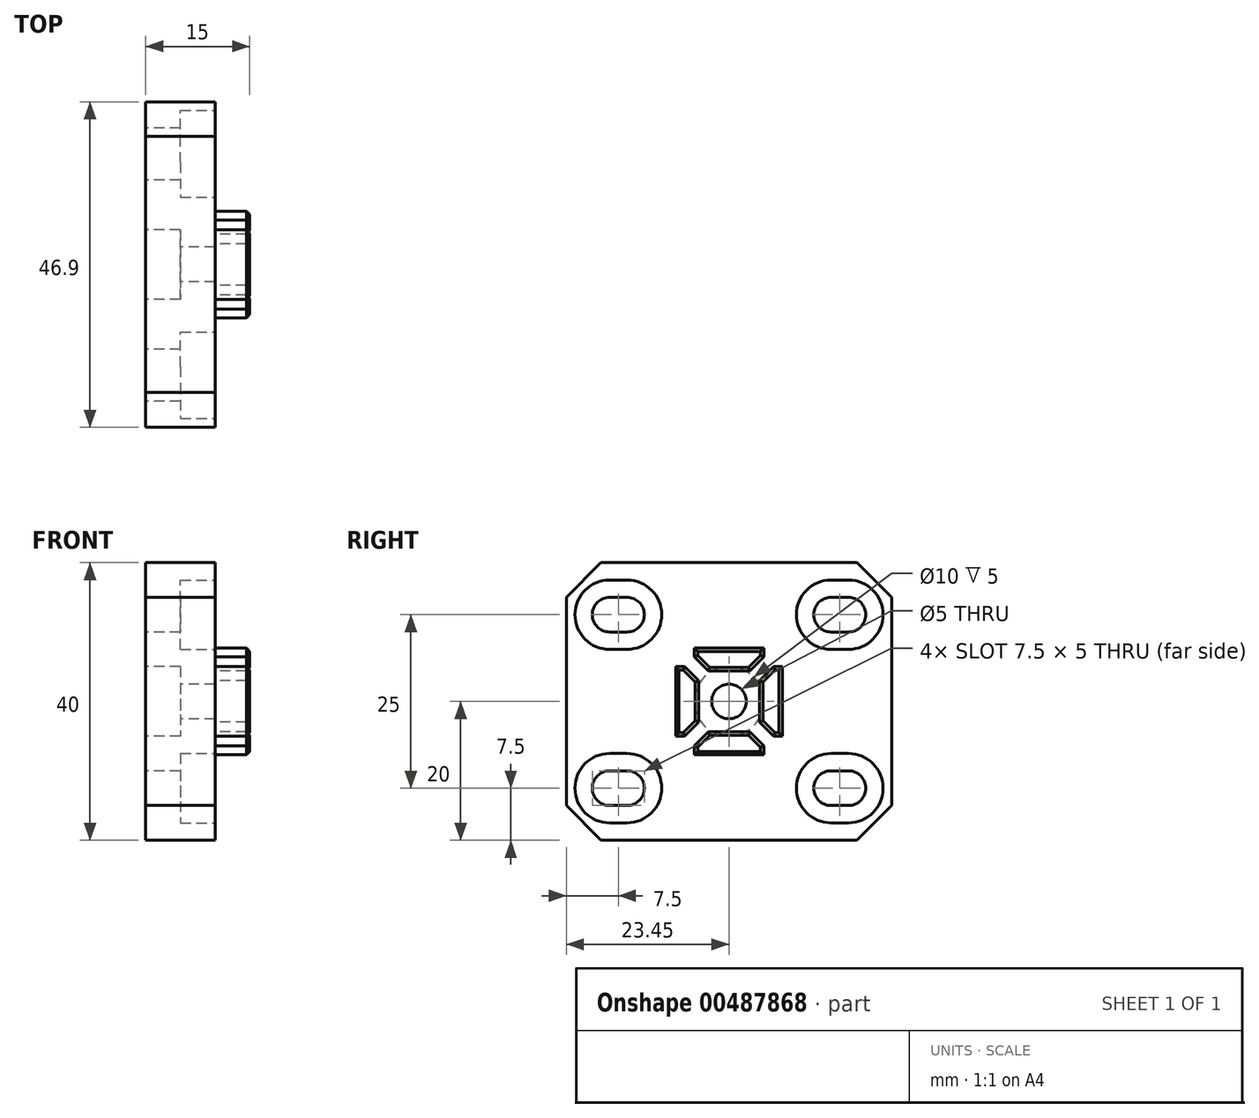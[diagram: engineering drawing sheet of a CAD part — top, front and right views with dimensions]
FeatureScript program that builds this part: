
annotation { "Feature Type Name" : "Feature", "Feature Type Description" : "" }
export const myFeature = defineFeature(function(context is Context, id is Id, definition is map)
    precondition{}
    {
        {
            var Q0;
            Q0=qCreatedBy(makeId("Right.planeOp"),FACE);
            var sketch = newSketch(context, id + "F0", { "sketchPlane" : qUnion([Q0])});
            skLineSegment(sketch, "E0.bottom", {"start": v(23.45, 20) * mm, "end": v(-23.45, 20) * mm});
            skLineSegment(sketch, "E0.top", {"start": v(23.45, -20) * mm, "end": v(-23.45, -20) * mm});
            skLineSegment(sketch, "E0.left", {"start": v(23.45, 20) * mm, "end": v(23.45, -20) * mm});
            skLineSegment(sketch, "E0.right", {"start": v(-23.45, 20) * mm, "end": v(-23.45, -20) * mm});
            skPoint(sketch, "E0.middle", {"position": v(0, 0) * mm});
            skLineSegment(sketch, "E1", {"start": v(15.95, 20) * mm, "end": v(15.95, -20) * mm, "construction": true});
            skLineSegment(sketch, "E2.MirrorCS", {"start": v(-15.95, 20) * mm, "end": v(-15.95, -20) * mm, "construction": true});
            skPoint(sketch, "E3", {"position": v(15.95, 12.5) * mm});
            skLineSegment(sketch, "E4", {"start": v(14.7, 12.5) * mm, "end": v(17.2, 12.5) * mm});
            skArc(sketch, "E5.0.startCap", {"start": v(14.7, 10) * mm, "mid": v(12.2, 12.5) * mm, "end": v(14.7, 15) * mm});
            skArc(sketch, "E5.0.endCap", {"start": v(17.2, 15) * mm, "mid": v(19.7, 12.5) * mm, "end": v(17.2, 10) * mm});
            skLineSegment(sketch, "E5.0.left", {"start": v(14.7, 15) * mm, "end": v(17.2, 15) * mm});
            skLineSegment(sketch, "E5.0.right", {"start": v(14.7, 10) * mm, "end": v(17.2, 10) * mm});
            skLineSegment(sketch, "E6.MirrorCS", {"start": v(14.7, -10) * mm, "end": v(17.2, -10) * mm});
            skArc(sketch, "E7.MirrorCS", {"start": v(14.7, -10) * mm, "mid": v(12.2, -12.5) * mm, "end": v(14.7, -15) * mm});
            skLineSegment(sketch, "E8.MirrorCS", {"start": v(14.7, -15) * mm, "end": v(17.2, -15) * mm});
            skArc(sketch, "E9.MirrorCS", {"start": v(17.2, -15) * mm, "mid": v(19.7, -12.5) * mm, "end": v(17.2, -10) * mm});
            skArc(sketch, "E10.MirrorCS", {"start": v(-14.7, 10) * mm, "mid": v(-12.2, 12.5) * mm, "end": v(-14.7, 15) * mm});
            skLineSegment(sketch, "E11.MirrorCS", {"start": v(-14.7, 15) * mm, "end": v(-17.2, 15) * mm});
            skLineSegment(sketch, "E12.MirrorCS", {"start": v(-14.7, 10) * mm, "end": v(-17.2, 10) * mm});
            skArc(sketch, "E13.MirrorCS", {"start": v(-17.2, 15) * mm, "mid": v(-19.7, 12.5) * mm, "end": v(-17.2, 10) * mm});
            skArc(sketch, "E14.MirrorCS", {"start": v(-17.2, -15) * mm, "mid": v(-19.7, -12.5) * mm, "end": v(-17.2, -10) * mm});
            skArc(sketch, "E15.MirrorCS", {"start": v(-14.7, -10) * mm, "mid": v(-12.2, -12.5) * mm, "end": v(-14.7, -15) * mm});
            skLineSegment(sketch, "E16.MirrorCS", {"start": v(-14.7, -10) * mm, "end": v(-17.2, -10) * mm});
            skLineSegment(sketch, "E17.MirrorCS", {"start": v(-14.7, -15) * mm, "end": v(-17.2, -15) * mm});
            skSolve(sketch);
        }
        {
            var Q0;
            Q0 = qSketchRegion(id + "F0", true);
            extrude(context, id + "F1", {"entities" : qUnion([Q0]), "depth" : 10 * mm, "offsetDistance" : 25 * mm});
        }
        {
            var Q0;
            Q0=makeQuery(id+"F1.opExtrude","SWEPT_EDGE",EDGE,{"disambiguationData":[OSD([sQuery(id+"F0.wireOp",EDGE,"E0.top"),sQuery(id+"F0.wireOp",EDGE,"E0.right")])]});
            var Q1;
            Q1=makeQuery(id+"F1.opExtrude","SWEPT_EDGE",EDGE,{"disambiguationData":[OSD([sQuery(id+"F0.wireOp",EDGE,"E0.bottom"),sQuery(id+"F0.wireOp",EDGE,"E0.right")])]});
            var Q2;
            Q2=makeQuery(id+"F1.opExtrude","SWEPT_EDGE",EDGE,{"disambiguationData":[OSD([sQuery(id+"F0.wireOp",EDGE,"E0.top"),sQuery(id+"F0.wireOp",EDGE,"E0.left")])]});
            var Q3;
            Q3=makeQuery(id+"F1.opExtrude","SWEPT_EDGE",EDGE,{"disambiguationData":[OSD([sQuery(id+"F0.wireOp",EDGE,"E0.bottom"),sQuery(id+"F0.wireOp",EDGE,"E0.left")])]});
            chamfer(context, id + "F2", {"entities" : qUnion([Q0, Q1, Q2, Q3]), "width" : 5 * mm, "tangentPropagation" : true});
        }
        {
            var Q0;
            Q0=makeQuery(id+"F1.opExtrude","CAP_FACE",FACE,{"disambiguationData":[OSD([sQuery(id+"F0.wireOp",EDGE,"E0.bottom"),sQuery(id+"F0.wireOp",EDGE,"E0.top"),sQuery(id+"F0.wireOp",EDGE,"E0.left"),sQuery(id+"F0.wireOp",EDGE,"E0.right"),sQuery(id+"F0.wireOp",EDGE,"vEGldzth-BNot-EE06-FjDa-u7C4T4Rxaar0"),sQuery(id+"F0.wireOp",EDGE,"8f5e52c0-c5bd-47e3-8c42-6e8efec94a390.MirrorC"),sQuery(id+"F0.wireOp",EDGE,"cc45769c-cd99-4294-87e5-1dfb32ceec680.MirrorC"),sQuery(id+"F0.wireOp",EDGE,"455db4ad-4749-4a7d-a7f8-e3abbd936af90.MirrorC"),sQuery(id+"F0.wireOp",EDGE,"VSL9ucTP-lhVw-caRV-tPp0-PcmT2fpHIwPz")])],"isStart":false});
            var sketch = newSketch(context, id + "F3", { "sketchPlane" : qUnion([Q0])});
            skLineSegment(sketch, "E18", {"start": v(2.99, 4.4) * mm, "end": v(5, 6.41) * mm});
            skLineSegment(sketch, "E19", {"start": v(5, 6.41) * mm, "end": v(5, 7.7) * mm});
            skLineSegment(sketch, "E20", {"start": v(-5, 7.7) * mm, "end": v(-5, 6.41) * mm});
            skLineSegment(sketch, "E21", {"start": v(-5, 6.41) * mm, "end": v(-2.99, 4.4) * mm});
            skLineSegment(sketch, "E22", {"start": v(2.99, 4.4) * mm, "end": v(0, 4.4) * mm});
            skLineSegment(sketch, "E23", {"start": v(0, 4.4) * mm, "end": v(-2.99, 4.4) * mm});
            skLineSegment(sketch, "E24", {"start": v(-5, 7.7) * mm, "end": v(5, 7.7) * mm});
            skLineSegment(sketch, "E25.1.0", {"start": v(-7.7, -5) * mm, "end": v(-7.7, 5) * mm});
            skLineSegment(sketch, "E25.1.1", {"start": v(-4.4, 0) * mm, "end": v(-4.4, -2.99) * mm});
            skLineSegment(sketch, "E25.1.2", {"start": v(-4.4, 2.99) * mm, "end": v(-4.4, 0) * mm});
            skLineSegment(sketch, "E25.1.3", {"start": v(-6.41, -5) * mm, "end": v(-4.4, -2.99) * mm});
            skLineSegment(sketch, "E25.1.4", {"start": v(-7.7, -5) * mm, "end": v(-6.41, -5) * mm});
            skLineSegment(sketch, "E25.1.5", {"start": v(-6.41, 5) * mm, "end": v(-7.7, 5) * mm});
            skLineSegment(sketch, "E25.1.6", {"start": v(-4.4, 2.99) * mm, "end": v(-6.41, 5) * mm});
            skLineSegment(sketch, "E25.2.0", {"start": v(5, -7.7) * mm, "end": v(-5, -7.7) * mm});
            skLineSegment(sketch, "E25.2.1", {"start": v(0, -4.4) * mm, "end": v(2.99, -4.4) * mm});
            skLineSegment(sketch, "E25.2.2", {"start": v(-2.99, -4.4) * mm, "end": v(0, -4.4) * mm});
            skLineSegment(sketch, "E25.2.3", {"start": v(5, -6.41) * mm, "end": v(2.99, -4.4) * mm});
            skLineSegment(sketch, "E25.2.4", {"start": v(5, -7.7) * mm, "end": v(5, -6.41) * mm});
            skLineSegment(sketch, "E25.2.5", {"start": v(-5, -6.41) * mm, "end": v(-5, -7.7) * mm});
            skLineSegment(sketch, "E25.2.6", {"start": v(-2.99, -4.4) * mm, "end": v(-5, -6.41) * mm});
            skLineSegment(sketch, "E25.3.0", {"start": v(7.7, 5) * mm, "end": v(7.7, -5) * mm});
            skLineSegment(sketch, "E25.3.1", {"start": v(4.4, 0) * mm, "end": v(4.4, 2.99) * mm});
            skLineSegment(sketch, "E25.3.2", {"start": v(4.4, -2.99) * mm, "end": v(4.4, 0) * mm});
            skLineSegment(sketch, "E25.3.3", {"start": v(6.41, 5) * mm, "end": v(4.4, 2.99) * mm});
            skLineSegment(sketch, "E25.3.4", {"start": v(7.7, 5) * mm, "end": v(6.41, 5) * mm});
            skLineSegment(sketch, "E25.3.5", {"start": v(6.41, -5) * mm, "end": v(7.7, -5) * mm});
            skLineSegment(sketch, "E25.3.6", {"start": v(4.4, -2.99) * mm, "end": v(6.41, -5) * mm});
            skPoint(sketch, "E25.center", {"position": v(0, 0) * mm});
            skSolve(sketch);
        }
        {
            var Q0;
            Q0 = qSketchRegion(id + "F3", true);
            extrude(context, id + "F4", {"entities" : qUnion([Q0]), "operationType" : NewBodyOperationType.ADD, "depth" : 5 * mm, "offsetDistance" : 25 * mm});
        }
        {
            var Q0;
            Q0=makeQuery(id+"F4.opExtrude","CAP_FACE",FACE,{"disambiguationData":[OSD([sQuery(id+"F3.wireOp",EDGE,"E25.2.0"),sQuery(id+"F3.wireOp",EDGE,"E25.2.1"),sQuery(id+"F3.wireOp",EDGE,"E25.2.2"),sQuery(id+"F3.wireOp",EDGE,"E25.2.3"),sQuery(id+"F3.wireOp",EDGE,"E25.2.4"),sQuery(id+"F3.wireOp",EDGE,"E25.2.5"),sQuery(id+"F3.wireOp",EDGE,"E25.2.6")])],"isStart":false});
            var Q1;
            Q1=makeQuery(id+"F4.opExtrude","CAP_FACE",FACE,{"disambiguationData":[OSD([sQuery(id+"F3.wireOp",EDGE,"E25.1.0"),sQuery(id+"F3.wireOp",EDGE,"E25.1.1"),sQuery(id+"F3.wireOp",EDGE,"E25.1.2"),sQuery(id+"F3.wireOp",EDGE,"E25.1.3"),sQuery(id+"F3.wireOp",EDGE,"E25.1.4"),sQuery(id+"F3.wireOp",EDGE,"E25.1.5"),sQuery(id+"F3.wireOp",EDGE,"E25.1.6")])],"isStart":false});
            var Q2;
            Q2=makeQuery(id+"F4.opExtrude","CAP_FACE",FACE,{"disambiguationData":[OSD([sQuery(id+"F3.wireOp",EDGE,"E18"),sQuery(id+"F3.wireOp",EDGE,"E19"),sQuery(id+"F3.wireOp",EDGE,"E20"),sQuery(id+"F3.wireOp",EDGE,"E21"),sQuery(id+"F3.wireOp",EDGE,"E22"),sQuery(id+"F3.wireOp",EDGE,"E23"),sQuery(id+"F3.wireOp",EDGE,"E24")])],"isStart":false});
            var Q3;
            Q3=makeQuery(id+"F4.opExtrude","CAP_FACE",FACE,{"disambiguationData":[OSD([sQuery(id+"F3.wireOp",EDGE,"E25.3.0"),sQuery(id+"F3.wireOp",EDGE,"E25.3.1"),sQuery(id+"F3.wireOp",EDGE,"E25.3.2"),sQuery(id+"F3.wireOp",EDGE,"E25.3.3"),sQuery(id+"F3.wireOp",EDGE,"E25.3.4"),sQuery(id+"F3.wireOp",EDGE,"E25.3.5"),sQuery(id+"F3.wireOp",EDGE,"E25.3.6")])],"isStart":false});
            chamfer(context, id + "F5", {"entities" : qUnion([Q0, Q1, Q2, Q3]), "width" : 0.5 * mm, "tangentPropagation" : true});
        }
        {
            var Q0;
            Q0=makeQuery(id+"F1.opExtrude","CAP_FACE",FACE,{"disambiguationData":[OSD([sQuery(id+"F0.wireOp",EDGE,"E0.bottom"),sQuery(id+"F0.wireOp",EDGE,"E0.top"),sQuery(id+"F0.wireOp",EDGE,"E0.left"),sQuery(id+"F0.wireOp",EDGE,"E0.right"),sQuery(id+"F0.wireOp",EDGE,"vEGldzth-BNot-EE06-FjDa-u7C4T4Rxaar0"),sQuery(id+"F0.wireOp",EDGE,"8f5e52c0-c5bd-47e3-8c42-6e8efec94a390.MirrorC"),sQuery(id+"F0.wireOp",EDGE,"cc45769c-cd99-4294-87e5-1dfb32ceec680.MirrorC"),sQuery(id+"F0.wireOp",EDGE,"455db4ad-4749-4a7d-a7f8-e3abbd936af90.MirrorC")])],"isStart":true});
            var sketch = newSketch(context, id + "F6", { "sketchPlane" : qUnion([Q0])});
            skCircle(sketch, "E26", {"center": v(0, 0) * mm, "radius": 2.5 * mm});
            skCircle(sketch, "E27", {"center": v(0, 0) * mm, "radius": 5 * mm});
            skSolve(sketch);
        }
        {
            var Q0;
            Q0 = qSketchRegion(id + "F6", true);
            extrude(context, id + "F7", {"entities" : qUnion([Q0]), "operationType" : NewBodyOperationType.REMOVE, "oppositeDirection" : true, "depth" : 5 * mm, "offsetDistance" : 25 * mm});
        }
        {
            var Q0;
            Q0=makeQuery(id+"F7.boolean.opBoolean","SPLIT",FACE,{"disambiguationData":[TD([makeQuery(id+"F7.opExtrude","SWEPT_FACE",FACE,{"disambiguationData":[OSD([sQuery(id+"F6.wireOp",EDGE,"E26")])]})])],"derivedFrom":makeQuery(id+"F1.opExtrude","CAP_FACE",FACE,{"disambiguationData":[OSD([sQuery(id+"F0.wireOp",EDGE,"E0.bottom"),sQuery(id+"F0.wireOp",EDGE,"E0.top"),sQuery(id+"F0.wireOp",EDGE,"E0.left"),sQuery(id+"F0.wireOp",EDGE,"E0.right"),sQuery(id+"F0.wireOp",EDGE,"vEGldzth-BNot-EE06-FjDa-u7C4T4Rxaar0"),sQuery(id+"F0.wireOp",EDGE,"8f5e52c0-c5bd-47e3-8c42-6e8efec94a390.MirrorC"),sQuery(id+"F0.wireOp",EDGE,"cc45769c-cd99-4294-87e5-1dfb32ceec680.MirrorC"),sQuery(id+"F0.wireOp",EDGE,"455db4ad-4749-4a7d-a7f8-e3abbd936af90.MirrorC")])],"isStart":true})});
            extrude(context, id + "F8", {"entities" : qUnion([Q0]), "operationType" : NewBodyOperationType.REMOVE, "endBound" : BoundingType.THROUGH_ALL, "oppositeDirection" : true, "depth" : 25 * mm, "offsetDistance" : 25 * mm});
        }
        {
            var Q0;
            Q0=makeQuery(id+"F1.opExtrude","CAP_FACE",FACE,{"disambiguationData":[OSD([sQuery(id+"F0.wireOp",EDGE,"E0.bottom"),sQuery(id+"F0.wireOp",EDGE,"E0.top"),sQuery(id+"F0.wireOp",EDGE,"E0.left"),sQuery(id+"F0.wireOp",EDGE,"E0.right"),sQuery(id+"F0.wireOp",EDGE,"vEGldzth-BNot-EE06-FjDa-u7C4T4Rxaar0"),sQuery(id+"F0.wireOp",EDGE,"8f5e52c0-c5bd-47e3-8c42-6e8efec94a390.MirrorC"),sQuery(id+"F0.wireOp",EDGE,"cc45769c-cd99-4294-87e5-1dfb32ceec680.MirrorC"),sQuery(id+"F0.wireOp",EDGE,"455db4ad-4749-4a7d-a7f8-e3abbd936af90.MirrorC")])],"isStart":false});
            var sketch = newSketch(context, id + "F9", { "sketchPlane" : qUnion([Q0])});
            skLineSegment(sketch, "E28", {"start": v(-14.7, 12.5) * mm, "end": v(-17.2, 12.5) * mm});
            skLineSegment(sketch, "E29", {"start": v(-17.2, -12.5) * mm, "end": v(-14.7, -12.5) * mm});
            skLineSegment(sketch, "E30", {"start": v(14.7, -12.5) * mm, "end": v(17.2, -12.5) * mm});
            skLineSegment(sketch, "E31", {"start": v(17.2, 12.5) * mm, "end": v(14.7, 12.5) * mm});
            skArc(sketch, "E32.0.startCap", {"start": v(17.2, 17.5) * mm, "mid": v(22.2, 12.5) * mm, "end": v(17.2, 7.5) * mm});
            skArc(sketch, "E32.0.endCap", {"start": v(14.7, 7.5) * mm, "mid": v(9.7, 12.5) * mm, "end": v(14.7, 17.5) * mm});
            skLineSegment(sketch, "E32.0.left", {"start": v(17.2, 7.5) * mm, "end": v(14.7, 7.5) * mm});
            skLineSegment(sketch, "E32.0.right", {"start": v(17.2, 17.5) * mm, "end": v(14.7, 17.5) * mm});
            skArc(sketch, "E32.1.startCap", {"start": v(-14.7, 17.5) * mm, "mid": v(-9.7, 12.5) * mm, "end": v(-14.7, 7.5) * mm});
            skArc(sketch, "E32.1.endCap", {"start": v(-17.2, 7.5) * mm, "mid": v(-22.2, 12.5) * mm, "end": v(-17.2, 17.5) * mm});
            skLineSegment(sketch, "E32.1.left", {"start": v(-14.7, 7.5) * mm, "end": v(-17.2, 7.5) * mm});
            skLineSegment(sketch, "E32.1.right", {"start": v(-14.7, 17.5) * mm, "end": v(-17.2, 17.5) * mm});
            skArc(sketch, "E32.2.startCap", {"start": v(-17.2, -17.5) * mm, "mid": v(-22.2, -12.5) * mm, "end": v(-17.2, -7.5) * mm});
            skArc(sketch, "E32.2.endCap", {"start": v(-14.7, -7.5) * mm, "mid": v(-9.7, -12.5) * mm, "end": v(-14.7, -17.5) * mm});
            skLineSegment(sketch, "E32.2.left", {"start": v(-17.2, -7.5) * mm, "end": v(-14.7, -7.5) * mm});
            skLineSegment(sketch, "E32.2.right", {"start": v(-17.2, -17.5) * mm, "end": v(-14.7, -17.5) * mm});
            skArc(sketch, "E32.3.startCap", {"start": v(14.7, -17.5) * mm, "mid": v(9.7, -12.5) * mm, "end": v(14.7, -7.5) * mm});
            skArc(sketch, "E32.3.endCap", {"start": v(17.2, -7.5) * mm, "mid": v(22.2, -12.5) * mm, "end": v(17.2, -17.5) * mm});
            skLineSegment(sketch, "E32.3.left", {"start": v(14.7, -7.5) * mm, "end": v(17.2, -7.5) * mm});
            skLineSegment(sketch, "E32.3.right", {"start": v(14.7, -17.5) * mm, "end": v(17.2, -17.5) * mm});
            skSolve(sketch);
        }
        {
            var Q0;
            Q0 = qSketchRegion(id + "F9", true);
            extrude(context, id + "F10", {"entities" : qUnion([Q0]), "operationType" : NewBodyOperationType.REMOVE, "oppositeDirection" : true, "depth" : 5 * mm, "offsetDistance" : 25 * mm});
        }
    });
